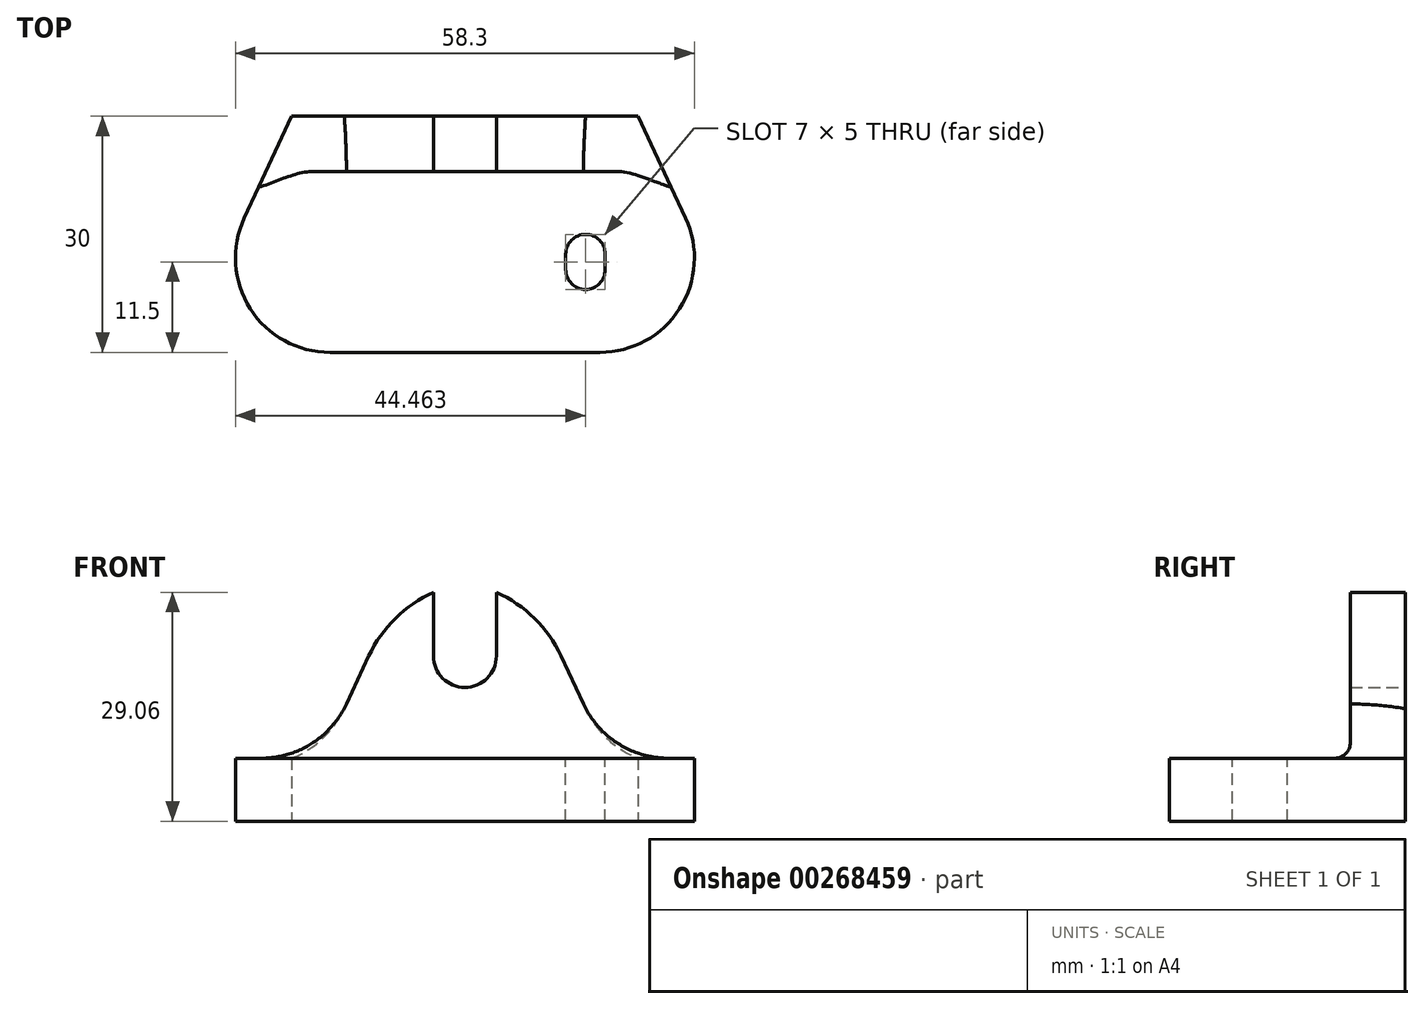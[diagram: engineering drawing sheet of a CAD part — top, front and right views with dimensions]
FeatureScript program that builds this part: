
annotation { "Feature Type Name" : "Feature", "Feature Type Description" : "" }
export const myFeature = defineFeature(function(context is Context, id is Id, definition is map)
    precondition{}
    {
        {
            var Q0;
            Q0=qCreatedBy(makeId("Front.planeOp"),FACE);
            var sketch = newSketch(context, id + "F0", { "sketchPlane" : qUnion([Q0])});
            skCircle(sketch, "E0", {"center": v(0, 21) * mm, "radius": 4 * mm});
            skLineSegment(sketch, "E1", {"start": v(0, 25) * mm, "end": v(14.28, 25) * mm, "construction": true});
            skCircle(sketch, "E2", {"center": v(0, 21) * mm, "radius": 9 * mm, "construction": true});
            skLineSegment(sketch, "E3", {"start": v(-4, 21) * mm, "end": v(-4, 29.06) * mm});
            skLineSegment(sketch, "E4", {"start": v(-12.2, 21) * mm, "end": v(-22, 0) * mm});
            skArc(sketch, "E5", {"start": v(-4, 29.06) * mm, "mid": v(-8.83, 25.77) * mm, "end": v(-12.2, 21) * mm});
            skLineSegment(sketch, "E6", {"start": v(-22, 0) * mm, "end": v(0, 0) * mm});
            skLineSegment(sketch, "E7", {"start": v(0, 0) * mm, "end": v(0, 21) * mm, "construction": true});
            skLineSegment(sketch, "E8.MirrorCS", {"start": v(4, 21) * mm, "end": v(4, 29.06) * mm});
            skArc(sketch, "E9.MirrorCS", {"start": v(4, 29.06) * mm, "mid": v(8.83, 25.77) * mm, "end": v(12.2, 21) * mm});
            skLineSegment(sketch, "E10.MirrorCS", {"start": v(12.2, 21) * mm, "end": v(22, 0) * mm});
            skLineSegment(sketch, "E11.MirrorCS", {"start": v(22, 0) * mm, "end": v(0, 0) * mm});
            skSolve(sketch);
        }
        {
            var Q0;
            {var subQ0=sQuery(id+"F0.wireOp",EDGE,"E3");Q0=makeQuery(id+"F0.imprint","IMPRINT",FACE,{"disambiguationData":[TD([[makeQuery(id+"F0.imprint","IMPRINT",EDGE,{"derivedFrom":subQ0}),1.0]])]});}
            extrude(context, id + "F1", {"entities" : qUnion([Q0]), "depth" : 7 * mm, "offsetDistance" : 25 * mm});
        }
        {
            var Q0;
            Q0=makeQuery(id+"F1.opExtrude","SWEPT_FACE",FACE,{"disambiguationData":[OSD([sQuery(id+"F0.wireOp",EDGE,"E6"),sQuery(id+"F0.wireOp",EDGE,"E11.MirrorCS")])]});
            var sketch = newSketch(context, id + "F2", { "sketchPlane" : qUnion([Q0])});
            skLineSegment(sketch, "E12", {"start": v(0, 0) * mm, "end": v(0, 53.04) * mm, "construction": true});
            skLineSegment(sketch, "E13", {"start": v(22, 0) * mm, "end": v(35.99, 30) * mm});
            skLineSegment(sketch, "E14", {"start": v(35.99, 30) * mm, "end": v(0, 30) * mm});
            skLineSegment(sketch, "E15.MirrorCS", {"start": v(-22, 0) * mm, "end": v(-35.99, 30) * mm});
            skLineSegment(sketch, "E16.MirrorCS", {"start": v(-35.99, 30) * mm, "end": v(0, 30) * mm});
            skSolve(sketch);
        }
        {
            var Q0;
            Q0=makeQuery(id+"F2.imprint","IMPRINT",FACE,{"disambiguationData":[TD([[makeQuery(id+"F2.imprint","IMPRINT",EDGE,{"derivedFrom":sQuery(id+"F2.wireOp",EDGE,"E13")}),1.0]])]});
            var Q1;
            {var subQ0=sQuery(id+"F0.wireOp",EDGE,"E6");Q1=makeQuery(id+"F2.imprint","IMPRINT",FACE,{"disambiguationData":[TD([[makeQuery(id+"F2.imprint","IMPRINT",EDGE,{"derivedFrom":makeQuery(id+"F1.opExtrude","SWEPT_EDGE",EDGE,{"disambiguationData":[OSD([sQuery(id+"F0.wireOp",EDGE,"E4"),subQ0])]})}),1.0]])]});}
            extrude(context, id + "F3", {"entities" : qUnion([Q0, Q1]), "operationType" : NewBodyOperationType.ADD, "oppositeDirection" : true, "depth" : 8 * mm, "offsetDistance" : 25 * mm});
        }
        {
            var Q0;
            Q0=makeQuery(id+"F3.opExtrude","CAP_FACE",FACE,{"disambiguationData":[OSD([sQuery(id+"F0.wireOp",EDGE,"E6"),sQuery(id+"F0.wireOp",EDGE,"E11.MirrorCS"),sQuery(id+"F2.wireOp",EDGE,"E13"),sQuery(id+"F2.wireOp",EDGE,"E14"),sQuery(id+"F2.wireOp",EDGE,"E15.MirrorCS"),sQuery(id+"F2.wireOp",EDGE,"E16.MirrorCS")])],"isStart":false});
            var sketch = newSketch(context, id + "F4", { "sketchPlane" : qUnion([Q0])});
            skLineSegment(sketch, "E17", {"start": v(0, -30) * mm, "end": v(0, -7) * mm, "construction": true});
            skLineSegment(sketch, "E18", {"start": v(0, -18.5) * mm, "end": v(30.63, -18.5) * mm, "construction": true});
            skLineSegment(sketch, "E19", {"start": v(15.31, -18.5) * mm, "end": v(15.31, -17.5) * mm, "construction": true});
            skArc(sketch, "E20", {"start": v(17.81, -17.5) * mm, "mid": v(15.31, -15) * mm, "end": v(12.81, -17.5) * mm});
            skArc(sketch, "E21.MirrorC", {"start": v(17.81, -19.5) * mm, "mid": v(15.31, -22) * mm, "end": v(12.81, -19.5) * mm});
            skLineSegment(sketch, "E22", {"start": v(12.81, -17.5) * mm, "end": v(12.81, -19.5) * mm});
            skLineSegment(sketch, "E23", {"start": v(17.81, -19.5) * mm, "end": v(17.81, -17.5) * mm});
            skLineSegment(sketch, "E24.bottom", {"start": v(-4, -7) * mm, "end": v(4, -7) * mm});
            skLineSegment(sketch, "E24.top", {"start": v(-4, -30) * mm, "end": v(4, -30) * mm});
            skLineSegment(sketch, "E24.left", {"start": v(-4, -7) * mm, "end": v(-4, -30) * mm});
            skLineSegment(sketch, "E24.right", {"start": v(4, -7) * mm, "end": v(4, -30) * mm});
            skPoint(sketch, "E24.middle", {"position": v(0, -18.5) * mm});
            skSolve(sketch);
        }
        {
            var Q0;
            Q0=makeQuery(id+"F4.imprint","IMPRINT",FACE,{"disambiguationData":[TD([[makeQuery(id+"F4.imprint","IMPRINT",EDGE,{"derivedFrom":sQuery(id+"F4.wireOp",EDGE,"E20")}),1.0]])]});
            var Q1;
            {var subQ0=sQuery(id+"F0.wireOp",EDGE,"E11.MirrorCS");var subQ1=sQuery(id+"F0.wireOp",EDGE,"E6");Q1=makeQuery(id+"F3.boolean.opBoolean","MERGE",FACE,{"derivedFrom":[makeQuery(id+"F1.opExtrude","SWEPT_FACE",FACE,{"disambiguationData":[OSD([subQ1,subQ0])]}),makeQuery(id+"F3.opExtrude","CAP_FACE",FACE,{"disambiguationData":[OSD([subQ1,subQ0,sQuery(id+"F2.wireOp",EDGE,"E13"),sQuery(id+"F2.wireOp",EDGE,"E14"),sQuery(id+"F2.wireOp",EDGE,"E15.MirrorCS"),sQuery(id+"F2.wireOp",EDGE,"E16.MirrorCS")])],"isStart":true})]});}
            extrude(context, id + "F5", {"entities" : qUnion([Q0]), "operationType" : NewBodyOperationType.REMOVE, "endBound" : BoundingType.UP_TO_SURFACE, "oppositeDirection" : true, "depth" : 25 * mm, "endBoundEntityFace" : qUnion([Q1]), "offsetDistance" : 25 * mm});
        }
        {
            var Q0;
            Q0=makeQuery(id+"F3.opExtrude","SWEPT_EDGE",EDGE,{"disambiguationData":[OSD([sQuery(id+"F2.wireOp",EDGE,"E13"),sQuery(id+"F2.wireOp",EDGE,"E14")])]});
            var Q1;
            Q1=makeQuery(id+"F3.opExtrude","SWEPT_EDGE",EDGE,{"disambiguationData":[OSD([sQuery(id+"F2.wireOp",EDGE,"E15.MirrorCS"),sQuery(id+"F2.wireOp",EDGE,"E16.MirrorCS")])]});
            var Q2;
            Q2=makeQuery(id+"F3.boolean.opBoolean","INTERSECT",EDGE,{"derivedFrom":[makeQuery(id+"F1.opExtrude","SWEPT_FACE",FACE,{"disambiguationData":[OSD([sQuery(id+"F0.wireOp",EDGE,"E10.MirrorCS")])]}),makeQuery(id+"F3.opExtrude","CAP_FACE",FACE,{"disambiguationData":[OSD([sQuery(id+"F0.wireOp",EDGE,"E6"),sQuery(id+"F0.wireOp",EDGE,"E11.MirrorCS"),sQuery(id+"F2.wireOp",EDGE,"E13"),sQuery(id+"F2.wireOp",EDGE,"E14"),sQuery(id+"F2.wireOp",EDGE,"E15.MirrorCS"),sQuery(id+"F2.wireOp",EDGE,"E16.MirrorCS")])],"isStart":false})]});
            var Q3;
            Q3=makeQuery(id+"F3.boolean.opBoolean","INTERSECT",EDGE,{"derivedFrom":[makeQuery(id+"F1.opExtrude","SWEPT_FACE",FACE,{"disambiguationData":[OSD([sQuery(id+"F0.wireOp",EDGE,"E4")])]}),makeQuery(id+"F3.opExtrude","CAP_FACE",FACE,{"disambiguationData":[OSD([sQuery(id+"F0.wireOp",EDGE,"E6"),sQuery(id+"F0.wireOp",EDGE,"E11.MirrorCS"),sQuery(id+"F2.wireOp",EDGE,"E13"),sQuery(id+"F2.wireOp",EDGE,"E14"),sQuery(id+"F2.wireOp",EDGE,"E15.MirrorCS"),sQuery(id+"F2.wireOp",EDGE,"E16.MirrorCS")])],"isStart":false})]});
            fillet(context, id + "F6", {"entities" : qUnion([Q0, Q1, Q2, Q3]), "tangentPropagation" : true, "radius" : 12 * mm, "defaultsChanged" : true, "vertexSettings" : [], "allowEdgeOverflow" : false});
        }
        {
            var Q0;
            {var subQ0=sQuery(id+"F0.wireOp",EDGE,"E11.MirrorCS");var subQ1=sQuery(id+"F0.wireOp",EDGE,"E6");Q0=makeQuery(id+"F3.boolean.opBoolean","INTERSECT",EDGE,{"derivedFrom":[makeQuery(id+"F1.opExtrude","CAP_FACE",FACE,{"disambiguationData":[OSD([sQuery(id+"F0.wireOp",EDGE,"E0"),sQuery(id+"F0.wireOp",EDGE,"E3"),sQuery(id+"F0.wireOp",EDGE,"E4"),sQuery(id+"F0.wireOp",EDGE,"E5"),subQ1,sQuery(id+"F0.wireOp",EDGE,"E8.MirrorCS"),sQuery(id+"F0.wireOp",EDGE,"E9.MirrorCS"),sQuery(id+"F0.wireOp",EDGE,"E10.MirrorCS"),subQ0])],"isStart":false}),makeQuery(id+"F3.opExtrude","CAP_FACE",FACE,{"disambiguationData":[OSD([subQ1,subQ0,sQuery(id+"F2.wireOp",EDGE,"E13"),sQuery(id+"F2.wireOp",EDGE,"E14"),sQuery(id+"F2.wireOp",EDGE,"E15.MirrorCS"),sQuery(id+"F2.wireOp",EDGE,"E16.MirrorCS")])],"isStart":false})]});}
            fillet(context, id + "F7", {"entities" : qUnion([Q0]), "tangentPropagation" : true, "radius" : 2 * mm, "defaultsChanged" : true, "vertexSettings" : [], "allowEdgeOverflow" : false});
        }
    });
